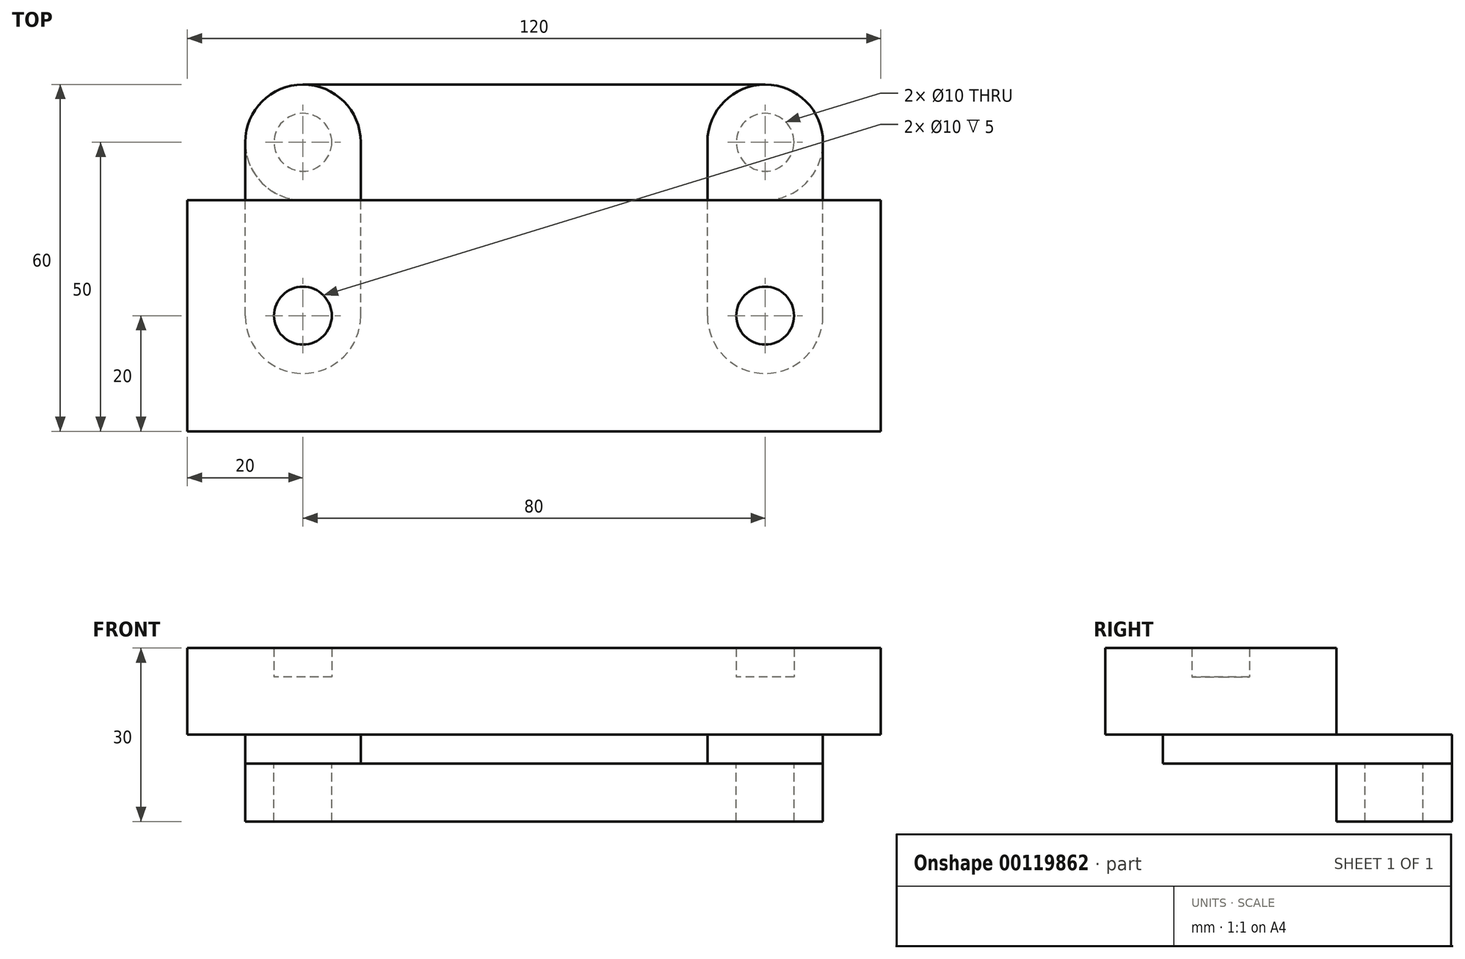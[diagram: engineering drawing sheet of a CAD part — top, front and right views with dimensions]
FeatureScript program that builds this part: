
annotation { "Feature Type Name" : "Feature", "Feature Type Description" : "" }
export const myFeature = defineFeature(function(context is Context, id is Id, definition is map)
    precondition{}
    {
        {
            var Q0;
            Q0=qCreatedBy(makeId("Top.planeOp"),FACE);
            var sketch = newSketch(context, id + "F0", { "sketchPlane" : qUnion([Q0])});
            skLineSegment(sketch, "E0.bottom", {"start": v(0, 0) * mm, "end": v(120, 0) * mm});
            skLineSegment(sketch, "E0.top", {"start": v(0, 40) * mm, "end": v(120, 40) * mm});
            skLineSegment(sketch, "E0.left", {"start": v(0, 0) * mm, "end": v(0, 40) * mm});
            skLineSegment(sketch, "E0.right", {"start": v(120, 0) * mm, "end": v(120, 40) * mm});
            skCircle(sketch, "E1", {"center": v(20, 20) * mm, "radius": 5 * mm});
            skCircle(sketch, "E2", {"center": v(100, 20) * mm, "radius": 5 * mm});
            skSolve(sketch);
        }
        {
            var Q0;
            Q0=makeQuery(id+"F0.imprint","IMPRINT",FACE,{"disambiguationData":[TD([[makeQuery(id+"F0.imprint","IMPRINT",EDGE,{"derivedFrom":sQuery(id+"F0.wireOp",EDGE,"E0.bottom")}),1.0]])]});
            extrude(context, id + "F1", {"entities" : qUnion([Q0]), "depth" : 15 * mm});
        }
        {
            var Q0;
            Q0=qCreatedBy(makeId("Top.planeOp"),FACE);
            var sketch = newSketch(context, id + "F2", { "sketchPlane" : qUnion([Q0])});
            skPoint(sketch, "E3.0", {"position": v(20, 20) * mm});
            skPoint(sketch, "E4.0", {"position": v(100, 20) * mm});
            skCircle(sketch, "E5.0", {"center": v(20, 20) * mm, "radius": 5 * mm});
            skCircle(sketch, "E6.0", {"center": v(100, 20) * mm, "radius": 5 * mm});
            skLineSegment(sketch, "E7", {"start": v(10.38, 20) * mm, "end": v(34.6, 20) * mm, "construction": true});
            skLineSegment(sketch, "E8", {"start": v(10, 20) * mm, "end": v(10, 50) * mm});
            skLineSegment(sketch, "E9", {"start": v(30, 20) * mm, "end": v(30, 50) * mm});
            skLineSegment(sketch, "E10", {"start": v(20, 65.56) * mm, "end": v(20, 5.94) * mm, "construction": true});
            skArc(sketch, "E11", {"start": v(30, 20) * mm, "mid": v(20, 10) * mm, "end": v(10, 20) * mm});
            skCircle(sketch, "E12", {"center": v(20, 50) * mm, "radius": 5 * mm});
            skArc(sketch, "E13", {"start": v(10, 50) * mm, "mid": v(20, 60) * mm, "end": v(30, 50) * mm});
            skLineSegment(sketch, "E14", {"start": v(100, 38.03) * mm, "end": v(100, 3.7) * mm, "construction": true});
            skLineSegment(sketch, "E15", {"start": v(86.68, 20) * mm, "end": v(123.4, 20) * mm, "construction": true});
            skLineSegment(sketch, "E16", {"start": v(90, 20) * mm, "end": v(90, 50) * mm});
            skLineSegment(sketch, "E17", {"start": v(110, 20) * mm, "end": v(110, 50) * mm});
            skArc(sketch, "E18", {"start": v(90, 20) * mm, "mid": v(100, 10) * mm, "end": v(110, 20) * mm});
            skArc(sketch, "E19", {"start": v(90, 50) * mm, "mid": v(100, 60) * mm, "end": v(110, 50) * mm});
            skCircle(sketch, "E20", {"center": v(100, 50) * mm, "radius": 5 * mm});
            skSolve(sketch);
        }
        {
            var Q0;
            Q0=makeQuery(id+"F2.imprint","IMPRINT",FACE,{"disambiguationData":[TD([[makeQuery(id+"F2.imprint","IMPRINT",EDGE,{"derivedFrom":sQuery(id+"F2.wireOp",EDGE,"E5.0")}),-1.0]])]});
            var Q1;
            Q1=makeQuery(id+"F2.imprint","IMPRINT",FACE,{"disambiguationData":[TD([[makeQuery(id+"F2.imprint","IMPRINT",EDGE,{"derivedFrom":sQuery(id+"F2.wireOp",EDGE,"E6.0")}),-1.0]])]});
            extrude(context, id + "F3", {"entities" : qUnion([Q0, Q1]), "oppositeDirection" : true, "depth" : 5 * mm});
        }
        {
            var Q0;
            Q0=makeQuery(id+"F2.imprint","IMPRINT",FACE,{"disambiguationData":[TD([[makeQuery(id+"F2.imprint","IMPRINT",EDGE,{"derivedFrom":sQuery(id+"F2.wireOp",EDGE,"E5.0")}),1.0]])]});
            extrude(context, id + "F4", {"entities" : qUnion([Q0]), "operationType" : NewBodyOperationType.ADD, "depth" : 10 * mm, "hasSecondDirection" : true, "secondDirectionOppositeDirection" : true, "secondDirectionDepth" : 5 * mm});
        }
        {
            var Q0;
            Q0=makeQuery(id+"F2.imprint","IMPRINT",FACE,{"disambiguationData":[TD([[makeQuery(id+"F2.imprint","IMPRINT",EDGE,{"derivedFrom":sQuery(id+"F2.wireOp",EDGE,"E6.0")}),1.0]])]});
            extrude(context, id + "F5", {"entities" : qUnion([Q0]), "operationType" : NewBodyOperationType.ADD, "depth" : 10 * mm, "hasSecondDirection" : true, "secondDirectionOppositeDirection" : true, "secondDirectionDepth" : 5 * mm});
        }
        {
            var Q0;
            Q0=makeQuery(id+"F2.imprint","IMPRINT",FACE,{"disambiguationData":[TD([[makeQuery(id+"F2.imprint","IMPRINT",EDGE,{"derivedFrom":sQuery(id+"F2.wireOp",EDGE,"E12")}),1.0]])]});
            extrude(context, id + "F6", {"entities" : qUnion([Q0]), "operationType" : NewBodyOperationType.ADD, "oppositeDirection" : true, "depth" : 15 * mm});
        }
        {
            var Q0;
            Q0=makeQuery(id+"F2.imprint","IMPRINT",FACE,{"disambiguationData":[TD([[makeQuery(id+"F2.imprint","IMPRINT",EDGE,{"derivedFrom":sQuery(id+"F2.wireOp",EDGE,"E20")}),1.0]])]});
            extrude(context, id + "F7", {"entities" : qUnion([Q0]), "operationType" : NewBodyOperationType.ADD, "oppositeDirection" : true, "depth" : 15 * mm});
        }
        {
            var Q0;
            {var subQ0=sQuery(id+"F2.wireOp",EDGE,"E6.0");Q0=makeQuery(id+"F5.boolean.opBoolean","MERGE",FACE,{"derivedFrom":[makeQuery(id+"F3.opExtrude","CAP_FACE",FACE,{"disambiguationData":[OSD([subQ0,sQuery(id+"F2.wireOp",EDGE,"E16"),sQuery(id+"F2.wireOp",EDGE,"E17"),sQuery(id+"F2.wireOp",EDGE,"E18"),sQuery(id+"F2.wireOp",EDGE,"E19"),sQuery(id+"F2.wireOp",EDGE,"E20")])],"isStart":false}),makeQuery(id+"F5.opExtrude","CAP_FACE",FACE,{"disambiguationData":[OSD([subQ0])],"isStart":true})]});}
            cPlane(context, id + "F8", {"entities" : qUnion([Q0]), "cplaneType" : CPlaneType.OFFSET, "offset" : 0 * mm, "width" : 150 * mm, "height" : 150 * mm});
        }
        {
            var Q0;
            Q0=qCreatedBy(id+"F8.planeOp",FACE);
            var sketch = newSketch(context, id + "F9", { "sketchPlane" : qUnion([Q0])});
            skPoint(sketch, "E21.0", {"position": v(100, -50) * mm});
            skPoint(sketch, "E22.0", {"position": v(20, -50) * mm});
            skLineSegment(sketch, "E23", {"start": v(100, -40) * mm, "end": v(20, -40) * mm});
            skLineSegment(sketch, "E24", {"start": v(100, -60) * mm, "end": v(20, -60) * mm});
            skLineSegment(sketch, "E25", {"start": v(100, -50) * mm, "end": v(20, -50) * mm, "construction": true});
            skArc(sketch, "E26", {"start": v(100, -40) * mm, "mid": v(110, -50) * mm, "end": v(100, -60) * mm});
            skArc(sketch, "E27", {"start": v(20, -40) * mm, "mid": v(10, -50) * mm, "end": v(20, -60) * mm});
            skCircle(sketch, "E28.0", {"center": v(100, -50) * mm, "radius": 5 * mm});
            skCircle(sketch, "E29.0", {"center": v(20, -50) * mm, "radius": 5 * mm});
            skSolve(sketch);
        }
        {
            var Q0;
            Q0=makeQuery(id+"F9.imprint","IMPRINT",FACE,{"disambiguationData":[TD([[makeQuery(id+"F9.imprint","IMPRINT",EDGE,{"derivedFrom":sQuery(id+"F9.wireOp",EDGE,"E23")}),1.0]])]});
            extrude(context, id + "F10", {"entities" : qUnion([Q0]), "depth" : 10 * mm});
        }
    });
